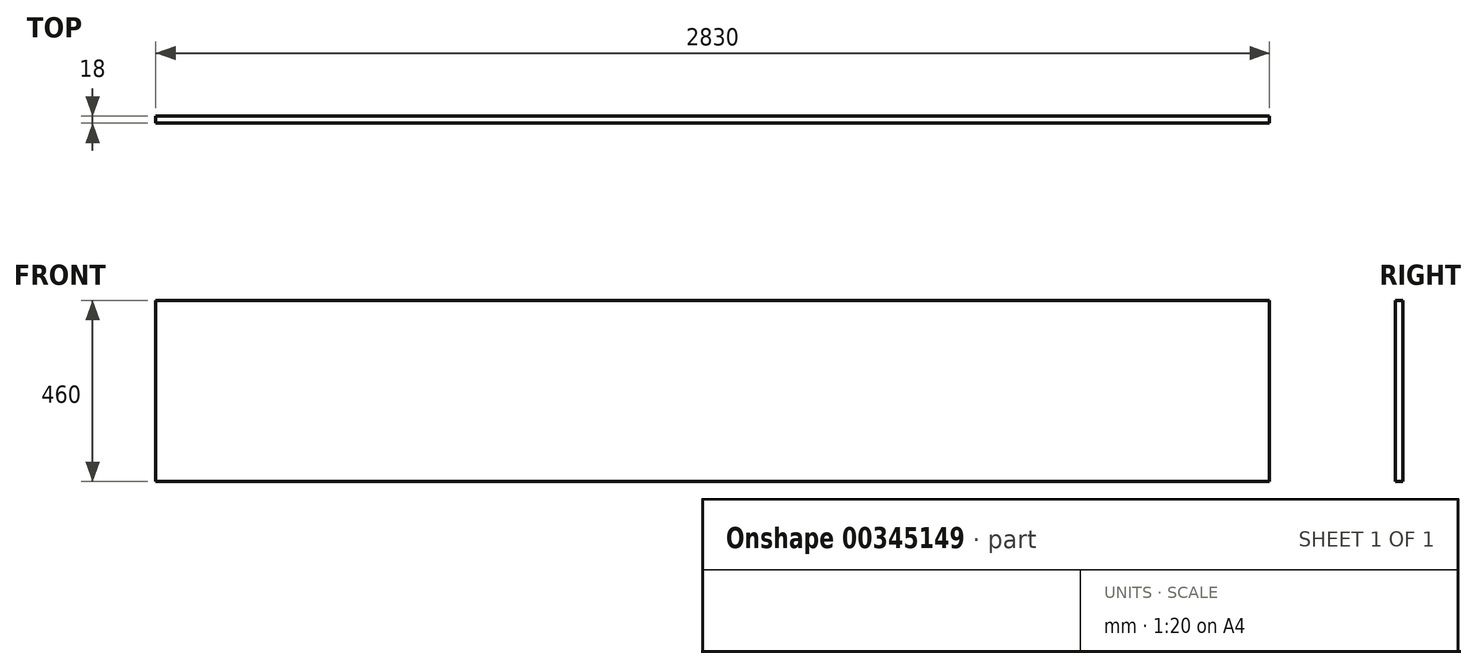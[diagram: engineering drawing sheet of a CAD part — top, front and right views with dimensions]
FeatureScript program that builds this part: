
annotation { "Feature Type Name" : "Feature", "Feature Type Description" : "" }
export const myFeature = defineFeature(function(context is Context, id is Id, definition is map)
    precondition{}
    {
        {
            var Q0;
            Q0=qCreatedBy(makeId("Front.planeOp"),FACE);
            var sketch = newSketch(context, id + "F0", { "sketchPlane" : qUnion([Q0])});
            skLineSegment(sketch, "E0.bottom", {"start": v(0, 0) * mm, "end": v(47.84, 0) * mm});
            skLineSegment(sketch, "E0.top", {"start": v(0, 47.87) * mm, "end": v(47.84, 47.87) * mm});
            skLineSegment(sketch, "E0.left", {"start": v(0, 0) * mm, "end": v(0, 47.87) * mm});
            skLineSegment(sketch, "E0.right", {"start": v(47.84, 0) * mm, "end": v(47.84, 47.87) * mm});
            skSolve(sketch);
        }
        {
            var Q0;
            Q0=makeQuery(id+"F0.imprint","IMPRINT",FACE,{"disambiguationData":[TD([[makeQuery(id+"F0.imprint","IMPRINT",EDGE,{"derivedFrom":sQuery(id+"F0.wireOp",EDGE,"E0.bottom")}),1.0]])]});
            extrude(context, id + "F1", {"entities" : qUnion([Q0]), "depth" : 18 * mm});
        }
        {
            var Q0;
            Q0=makeQuery(id+"F1.opExtrude","SWEPT_FACE",FACE,{"disambiguationData":[OSD([sQuery(id+"F0.wireOp",EDGE,"E0.left")])]});
            extrude(context, id + "F2", {"entities" : qUnion([Q0]), "operationType" : NewBodyOperationType.ADD, "oppositeDirection" : true, "depth" : 2830 * mm});
        }
        {
            var Q0;
            {var subQ0=sQuery(id+"F0.wireOp",EDGE,"E0.bottom");Q0=makeQuery(id+"F2.boolean.opBoolean","MERGE",FACE,{"derivedFrom":[makeQuery(id+"F1.opExtrude","SWEPT_FACE",FACE,{"disambiguationData":[OSD([subQ0])]}),makeQuery(id+"F2.opExtrude","SWEPT_FACE",FACE,{"disambiguationData":[OSD([subQ0,sQuery(id+"F0.wireOp",EDGE,"E0.left")])]})]});}
            extrude(context, id + "F3", {"entities" : qUnion([Q0]), "operationType" : NewBodyOperationType.ADD, "oppositeDirection" : true, "depth" : 500 * mm});
        }
        {
            var Q0;
            Q0=makeQuery(id+"F3.opExtrude","CAP_FACE",FACE,{"disambiguationData":[OSD([sQuery(id+"F0.wireOp",EDGE,"E0.bottom"),sQuery(id+"F0.wireOp",EDGE,"E0.left")])],"isStart":false});
            extrude(context, id + "F4", {"entities" : qUnion([Q0]), "operationType" : NewBodyOperationType.ADD, "oppositeDirection" : true, "depth" : 50 * mm});
        }
        {
            var Q0;
            Q0=makeQuery(id+"F3.opExtrude","CAP_FACE",FACE,{"disambiguationData":[OSD([sQuery(id+"F0.wireOp",EDGE,"E0.bottom"),sQuery(id+"F0.wireOp",EDGE,"E0.left")])],"isStart":false});
            extrude(context, id + "F5", {"entities" : qUnion([Q0]), "operationType" : NewBodyOperationType.REMOVE, "oppositeDirection" : true, "depth" : 50 * mm});
        }
        {
            var Q0;
            Q0=makeQuery(id+"F5.boolean.opBoolean","COPY",FACE,{"derivedFrom":makeQuery(id+"F5.opExtrude","CAP_FACE",FACE,{"disambiguationData":[OSD([sQuery(id+"F0.wireOp",EDGE,"E0.bottom"),sQuery(id+"F0.wireOp",EDGE,"E0.left")])],"isStart":false})});
            extrude(context, id + "F6", {"entities" : qUnion([Q0]), "operationType" : NewBodyOperationType.ADD, "depth" : 20 * mm});
        }
        {
            var Q0;
            Q0=makeQuery(id+"F6.opExtrude","CAP_FACE",FACE,{"disambiguationData":[OSD([sQuery(id+"F0.wireOp",EDGE,"E0.bottom"),sQuery(id+"F0.wireOp",EDGE,"E0.left")])],"isStart":false});
            extrude(context, id + "F7", {"entities" : qUnion([Q0]), "operationType" : NewBodyOperationType.REMOVE, "oppositeDirection" : true, "depth" : 10 * mm});
        }
    });
